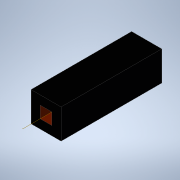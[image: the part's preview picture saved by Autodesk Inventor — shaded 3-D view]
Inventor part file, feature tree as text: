
AUTODESK INVENTOR PART (.ipt)
format: ipt  version: 2020 (Build 240168000, 168)  size: 99,328 bytes
history: native  units: in
note: dims shown in document units (in); Inventor stores cm internally (conversion verified against a paired STEP export)
features: other x2, plane x2
ambient origin geometry x8: Origin, YZ Plane, XZ Plane, XY Plane, X Axis, Y Axis, Z Axis, Center Point
bodies: Solid1 (feature_tree)
feature tree (4):
  other  "Cnt1"
  other  "Work Axis1"
  plane  "Work Plane1"
  plane  "Work Plane2"
